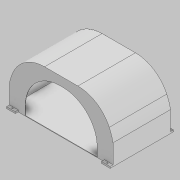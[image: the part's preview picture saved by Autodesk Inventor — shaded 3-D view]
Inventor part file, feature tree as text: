
AUTODESK INVENTOR PART (.ipt)
format: ipt  version: 2021 (Build 250183000, 183)  size: 217,600 bytes
history: native  units: mm
features: extrude x6, sketch x6, mirror x2, fillet x2, shell x1, plane x1
ambient origin geometry x8: Origin, YZ Plane, XZ Plane, XY Plane, X Axis, Y Axis, Z Axis, Center Point
bodies: Solid1 (feature_tree)
feature tree (18):
  extrude  "Extrusion1"  Depth=1000.0mm TaperAngle=0.0deg
  extrude  "Extrusion2"  Depth=1000.0mm
  mirror  "Mirror1"
  fillet  "Fillet1"  Radius=350.0mm
  sketch  "Sketch3"  dims[d9=0.0mm d10=600.0mm d11=150.0mm]
  shell  "Shell2"  Thickness=1000.0mm
  extrude  "Extrusion3"  Depth=600.0mm
  fillet  "Fillet2"  Radius=150.0mm
  extrude  "Extrusion4"  Depth=5.0mm
  extrude  "Extrusion5"  Depth=600.0mm
  extrude  "Extrusion6"  Depth=30.0mm
  mirror  "Mirror2"
  sketch  "Sketch1"  dims[d0=900.0mm d2=1000.0mm d3=0.0mm]
  sketch  "Sketch2"  dims[d5=900.0mm d6=550.0mm d7=350.0mm d8=1000.0mm]
  plane  "Work Plane1"
  sketch  "Sketch4"  dims[d12=600.0mm d13=5.0mm]
  sketch  "Sketch5"  dims[d14=10.0mm d15=0.0mm d16=600.0mm]
  sketch  "Sketch6"  dims[d17=10.0mm d18=0.0mm d19=30.0mm d20=150.0mm d23=50.0mm d24=0.0mm d25=20.0mm d29=30.0mm d30=0.0mm d31=1650.0mm d32=75.0mm]
